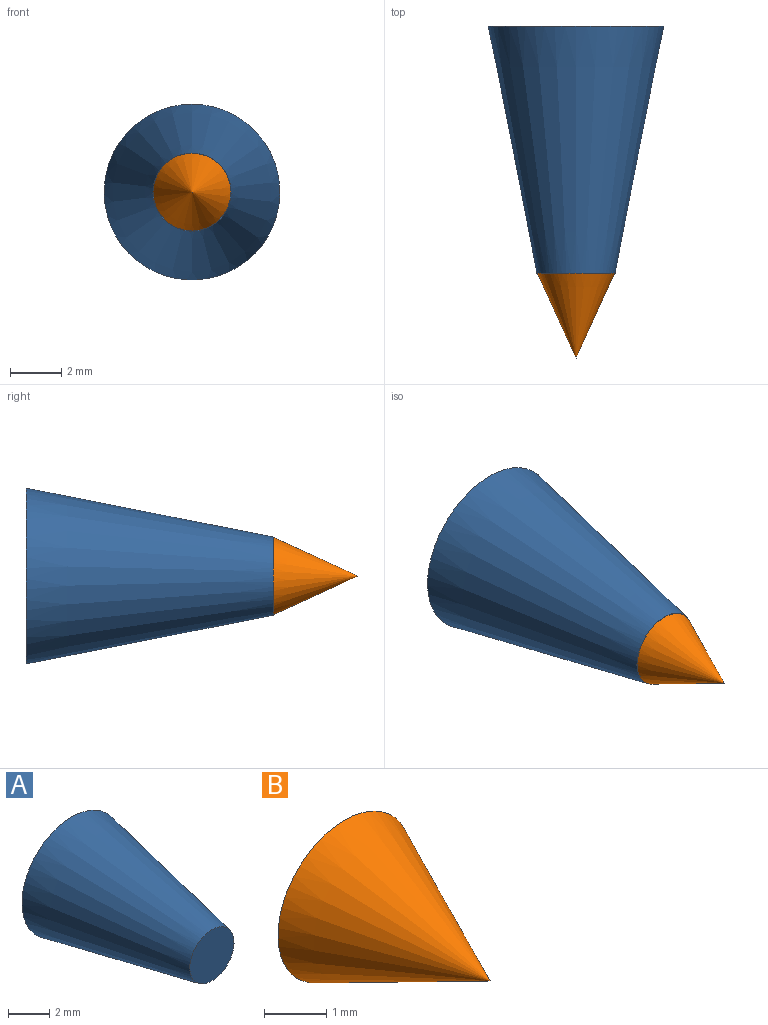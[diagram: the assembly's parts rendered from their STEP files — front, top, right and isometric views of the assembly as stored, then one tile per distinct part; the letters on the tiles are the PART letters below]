
ASSEMBLY  parts=2 mates=1
PART A: 3 faces, bbox 6.9x9.7x6.9 mm
  f0: plane 6.86x6.86mm, normal (0,1,0), area 36.9mm2, adj f2
  f1: plane 3.05x3.05mm, normal (0,-1,0), area 7.3mm2, adj f2
  f2: cone r=1.52mm half-angle=11.2deg, axis (0,1,0), area 153.1mm2, adj f0,f1
PART B: 2 faces, bbox 3x3.3x3 mm
  f0: cone r=0mm half-angle=24.6deg, axis (0,1,0), area 17.2mm2, adj f1
  f1: plane 3.02x3.02mm, normal (0,1,0), area 7.2mm2, adj f0
PLACE A t=(1.51,-2.48,0.68)mm
PLACE B t=(1.51,-2.48,0.7)mm
MATE parallel B.f0 <-> A.f2  axis (0,1,0) through (1.51,-2.48,2.21)mm
